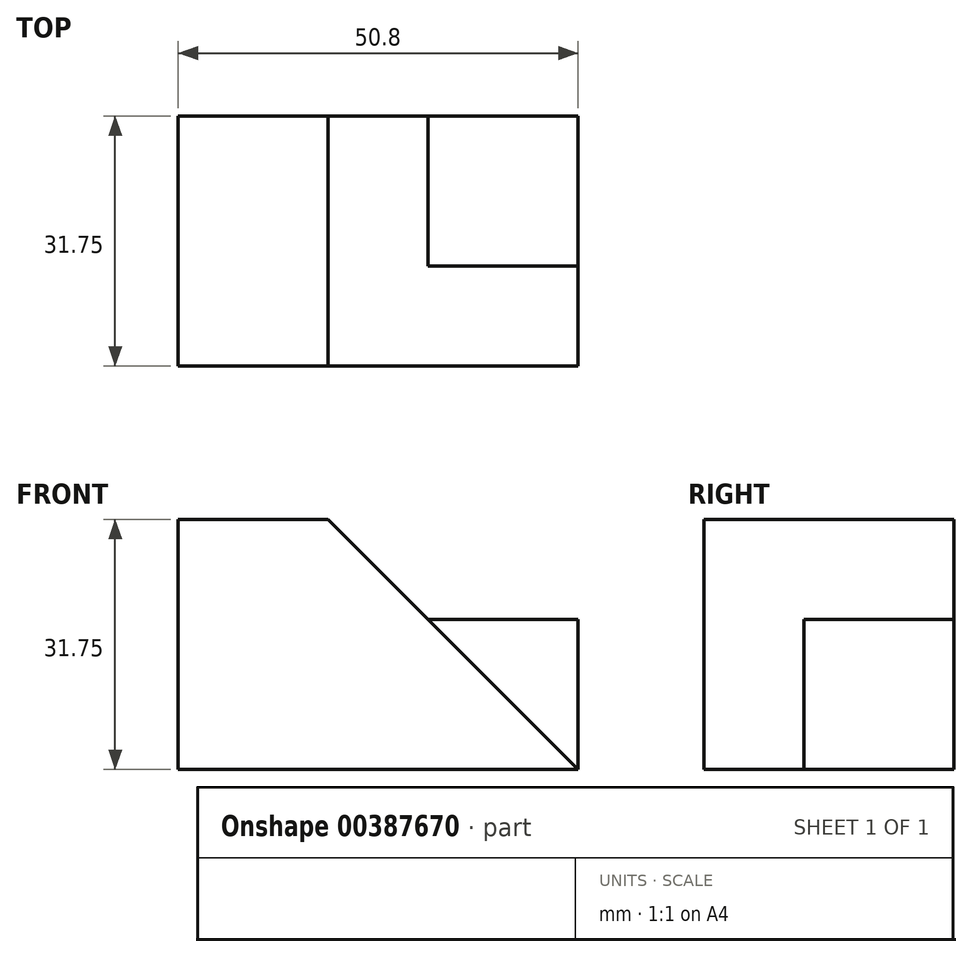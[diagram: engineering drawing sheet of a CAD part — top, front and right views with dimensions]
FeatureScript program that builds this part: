
annotation { "Feature Type Name" : "Feature", "Feature Type Description" : "" }
export const myFeature = defineFeature(function(context is Context, id is Id, definition is map)
    precondition{}
    {
        {
            var Q0;
            Q0=qCreatedBy(makeId("Front.planeOp"),FACE);
            var sketch = newSketch(context, id + "F0", { "sketchPlane" : qUnion([Q0])});
            skLineSegment(sketch, "E0", {"start": v(0, 0) * mm, "end": v(0, 31.75) * mm});
            skLineSegment(sketch, "E1", {"start": v(0, 31.75) * mm, "end": v(19.05, 31.75) * mm});
            skLineSegment(sketch, "E2", {"start": v(19.05, 31.75) * mm, "end": v(50.8, 0) * mm});
            skLineSegment(sketch, "E3", {"start": v(50.8, 0) * mm, "end": v(0, 0) * mm});
            skSolve(sketch);
        }
        {
            var Q0;
            Q0=makeQuery(id+"F0.imprint","IMPRINT",FACE,{"disambiguationData":[TD([[makeQuery(id+"F0.imprint","IMPRINT",EDGE,{"derivedFrom":sQuery(id+"F0.wireOp",EDGE,"E0")}),-1.0]])]});
            extrude(context, id + "F1", {"entities" : qUnion([Q0]), "depth" : 31.75 * mm});
        }
        {
            var Q0;
            Q0=qCreatedBy(makeId("Top.planeOp"),FACE);
            var sketch = newSketch(context, id + "F2", { "sketchPlane" : qUnion([Q0])});
            skLineSegment(sketch, "E4", {"start": v(50.8, 0) * mm, "end": v(50.8, -19.05) * mm});
            skLineSegment(sketch, "E5", {"start": v(50.8, -19.05) * mm, "end": v(31.75, -19.05) * mm});
            skLineSegment(sketch, "E6", {"start": v(31.75, -19.05) * mm, "end": v(31.75, 0) * mm});
            skLineSegment(sketch, "E7", {"start": v(31.75, 0) * mm, "end": v(50.8, 0) * mm});
            skSolve(sketch);
        }
        {
            var Q0;
            Q0=makeQuery(id+"F2.imprint","IMPRINT",FACE,{"disambiguationData":[TD([[makeQuery(id+"F2.imprint","IMPRINT",EDGE,{"derivedFrom":sQuery(id+"F2.wireOp",EDGE,"E4")}),-1.0]])]});
            extrude(context, id + "F3", {"entities" : qUnion([Q0]), "operationType" : NewBodyOperationType.ADD, "depth" : 19.05 * mm});
        }
    });
